# Revit family: ERXLL4080-619A^22
name_source: partatom
category: 照明器具
units: mm (PartAtom-declared; Revit-internal decimal feet)

## family parameters
パーツ タイプ = 標準
ロード時にボイドで切り取り = いいえ
丸型コネクタ寸法 = 直径を使用
作業面ベース = はい
光源 = いいえ
共有 = いいえ
常に垂直 = いいえ
部屋計算ポイント = はい

## types (1)
- ERXLL4080-619A^22
    Clearance Back = 0  [stored 0 ft]
    Clearance Bottom = 0  [stored 0 ft]
    Clearance Front = 0  [stored 0 ft]
    Clearance Left = 0  [stored 0 ft]
    Clearance Right = 0  [stored 0 ft]
    Clearance Top = 0  [stored 0 ft]
    Depth = 0  [stored 0 ft]
    Height = 0  [stored 0 ft]
    Width = 0  [stored 0 ft]
    カタログ番号 = HS001037
    ランプの種類 = LED
    仕上色 = 金屬
    光源寿命 = 60000
    取付脚 = 金屬
    定格光束(lm) = 13500 lm
    定格消費電力（200V時平均） = 76 W
    定格消費電力（200V時最大） = 0 W
    平均演色評価数(Ra) = 83
    形式1 = 投光器
    既定の高さ = 1219.2  [stored 4 ft]
    色温度 = 5000
    製品質量 = 10.20 kg
    製造元 = 伊東電機株式会社(ITO DENKI CO.,LTD.)

note: [stored X ft] marks values corroborated as IEEE doubles in the binary element streams (Revit-internal decimal feet)
